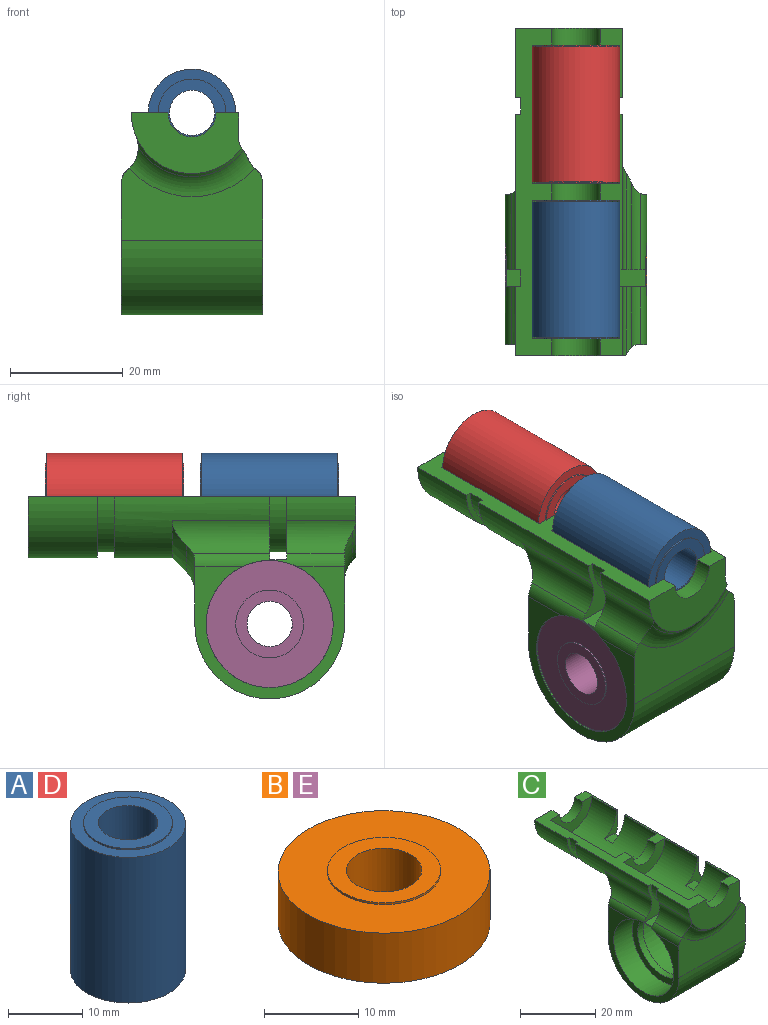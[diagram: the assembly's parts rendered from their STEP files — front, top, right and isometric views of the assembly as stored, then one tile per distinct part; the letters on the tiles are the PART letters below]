
ASSEMBLY  parts=5 mates=4
PART A: 8 faces, bbox 15.5x15.5x24.5 mm
  f0: cylinder r=6mm len=12mm, axis (0,0,-1), area 9.4mm2, adj f4,f7
  f1: cylinder r=4mm len=24.5mm, axis (0,0,-1), area 615.8mm2, adj f3,f4
  f2: cylinder r=6mm len=12mm, axis (0,0,-1), area 9.4mm2, adj f3,f6
  f3: plane 12x12mm, normal (0,0,1), area 62.8mm2, adj f1,f2
  f4: plane 12x12mm, normal (0,0,-1), area 62.8mm2, adj f0,f1
  f5: cylinder r=7.75mm len=24mm, axis (0,0,-1), area 1168.7mm2, adj f6,f7
  f6: plane 15.5x15.5mm, normal (0,0,1), area 75.6mm2, adj f2,f5
  f7: plane 15.5x15.5mm, normal (0,0,-1), area 75.6mm2, adj f0,f5
PART B: 8 faces, bbox 22.5x22.5x7 mm
  f0: cylinder r=6mm len=12mm, axis (0,0,-1), area 9.4mm2, adj f4,f7
  f1: cylinder r=4mm len=8mm, axis (0,0,-1), area 175.9mm2, adj f3,f4
  f2: cylinder r=6mm len=12mm, axis (0,0,-1), area 9.4mm2, adj f3,f6
  f3: plane 12x12mm, normal (0,0,1), area 62.8mm2, adj f1,f2
  f4: plane 12x12mm, normal (0,0,-1), area 62.8mm2, adj f0,f1
  f5: cylinder r=11.25mm len=22.5mm, axis (0,0,-1), area 459.5mm2, adj f6,f7
  f6: plane 22.5x22.5mm, normal (0,0,1), area 284.5mm2, adj f2,f5
  f7: plane 22.5x22.5mm, normal (0,0,-1), area 284.5mm2, adj f0,f5
PART C: 60 faces, bbox 32.8x58x35.8 mm
  f0: cylinder r=9.75mm len=16.54mm, axis (0,-1,0), area 68.5mm2, adj f5,f13,f28,f53
  f1: plane 19x10.75mm, normal (0,1,0), area 140.7mm2, adj f14,f15,f27,f28,f52,f57
  f2: plane 19.52x10.75mm, normal (0,-1,0), area 141.8mm2, adj f6,f23,f24,f28,f42,f49,f55
  f3: cylinder r=9.75mm len=16.54mm, axis (0,-1,0), area 68.5mm2, adj f4,f25,f28,f50
  f4: plane 24.45x11.15mm, normal (0,-1,0), area 84.8mm2, adj f3,f7,f9,f21,f26,f28,f31,f45
  f5: plane 19x10.75mm, normal (0,1,0), area 36mm2, adj f0,f7,f17,f26,f28,f51,f53,f54
  f6: plane 12.25x4mm, normal (0,0,1), area 16.6mm2, adj f2,f21,f22,f23,f25,f49
  f7: plane 27.5x4mm, normal (0,0,1), area 24.3mm2, adj f4,f5,f17,f18,f19,f20,f21,f51
  f8: torus R=14.82mm, axis (0,-1,0), area 90.2mm2, adj f10,f30,f42,f46,f59
  f9: cylinder r=5mm len=15.39mm, axis (0,-1,0), area 38.4mm2, adj f4,f43,f44,f47,f58
  f10: cylinder r=5mm len=10.77mm, axis (0,-1,0), area 27.9mm2, adj f8,f25,f30,f47,f59
  f11: cylinder r=9.25mm len=18.5mm, axis (-1,0,0), area 116.2mm2, adj f37,f39
  f12: cylinder r=11.25mm len=22.5mm, axis (-1,0,0), area 493.5mm2, adj f34,f37,f48
  f13: plane 19x10.75mm, normal (0,-1,0), area 36mm2, adj f0,f14,f17,f27,f28,f52,f53,f57
  f14: cylinder r=10.75mm len=16.83mm, axis (0,-1,0), area 286mm2, adj f1,f13,f28,f57
  f15: cylinder r=4.25mm len=8.5mm, axis (0,-1,0), area 40.1mm2, adj f1,f16,f27,f28
  f16: plane 15.5x7.75mm, normal (0,-1,0), area 66mm2, adj f15,f17,f27,f28
  f17: cylinder r=7.75mm len=24.5mm, axis (0,-1,0), area 570.3mm2, adj f5,f7,f13,f16,f18,f27,f28,f53
  f18: plane 15.5x7.75mm, normal (0,1,0), area 66mm2, adj f7,f17,f19,f28
  f19: cylinder r=4.25mm len=8.5mm, axis (0,-1,0), area 40.1mm2, adj f7,f18,f20,f28
  f20: plane 15.5x7.75mm, normal (0,-1,0), area 66mm2, adj f7,f19,f21,f28
  f21: cylinder r=7.75mm len=24.5mm, axis (0,-1,0), area 570.3mm2, adj f4,f6,f7,f20,f22,f25,f28,f50
  f22: plane 15.5x7.75mm, normal (0,1,0), area 66mm2, adj f6,f21,f23,f28
  f23: cylinder r=4.25mm len=8.5mm, axis (0,-1,0), area 40.1mm2, adj f2,f6,f22,f28
  f24: cylinder r=10.75mm len=12.25mm, axis (0,-1,0), area 52.9mm2, adj f2,f25,f28,f46
  f25: plane 24.45x11.15mm, normal (0,1,0), area 84.8mm2, adj f3,f6,f10,f21,f24,f28,f31,f46
  f26: cylinder r=10.75mm len=27.5mm, axis (0,-1,0), area 313.8mm2, adj f4,f5,f28,f43,f45,f56
  f27: plane 12.25x4mm, normal (0,0,1), area 16.6mm2, adj f1,f13,f15,f16,f17,f52
  f28: plane 58x6.5mm, normal (0,0,1), area 199.5mm2, adj f0,f1,f2,f3,f4,f5,f13,f14
  f29: plane 25x11.07mm, normal (0,1,0), area 184.6mm2, adj f33,f34,f41,f44,f47,f48
  f30: plane 25x12.68mm, normal (0,-1,0), area 237.8mm2, adj f8,f10,f33,f34,f41,f46,f47,f48
  f31: plane 24.45x3mm, normal (0,0,1), area 73.3mm2, adj f4,f25,f47,f48
  f32: cylinder r=11.25mm len=22.5mm, axis (-1,0,0), area 493.5mm2, adj f33,f36,f47
  f33: plane 26.5x23.34mm, normal (1,0,0), area 153.4mm2, adj f29,f30,f32,f41,f47
  f34: plane 26.5x23.34mm, normal (-1,0,0), area 153.4mm2, adj f12,f29,f30,f41,f48
  f35: cylinder r=9.25mm len=18.5mm, axis (-1,0,0), area 116.2mm2, adj f36,f40
  f36: plane 22.5x22.5mm, normal (1,0,0), area 128.8mm2, adj f32,f35
  f37: plane 22.5x22.5mm, normal (-1,0,0), area 128.8mm2, adj f11,f12
  f38: cylinder r=11.25mm len=22.5mm, axis (1,0,0), area 494.8mm2, adj f39,f40
  f39: plane 22.5x22.5mm, normal (1,0,0), area 128.8mm2, adj f11,f38
  f40: plane 22.5x22.5mm, normal (-1,0,0), area 128.8mm2, adj f35,f38
  f41: cylinder r=13.25mm len=26.5mm, axis (1,0,0), area 1040.7mm2, adj f29,f30,f33,f34
  f42: cone r=12.75mm half-angle=45deg, axis (0,1,0), area 16.7mm2, adj f2,f8,f46,f55,f59
  f43: cone r=10.75mm half-angle=45deg, axis (0,-1,0), area 81.5mm2, adj f9,f26,f44,f45,f54,f56,f58
  f44: torus R=16.82mm, axis (0,-1,0), area 99.4mm2, adj f9,f29,f43,f45,f47,f48
  f45: cylinder r=5mm len=17.25mm, axis (0,-1,0), area 101.6mm2, adj f4,f26,f43,f44,f48
  f46: cylinder r=5mm len=12.25mm, axis (0,-1,0), area 72.3mm2, adj f8,f24,f25,f30,f42,f48
  f47: cylinder r=3mm len=26.78mm, axis (0,-1,0), area 59.3mm2, adj f4,f9,f10,f25,f29,f30,f31,f32
  f48: cylinder r=3mm len=26.78mm, axis (0,-1,0), area 59.3mm2, adj f4,f12,f25,f29,f30,f31,f34,f44
  f49: plane 12.25x4.52mm, normal (1,0,0), area 55.3mm2, adj f2,f6,f25,f55
  f50: plane 3.46x3mm, normal (0,0,1), area 10.4mm2, adj f3,f4,f21,f25
  f51: plane 27.5x4.52mm, normal (1,0,0), area 124.2mm2, adj f4,f5,f7,f54
  f52: plane 12.25x4.74mm, normal (1,0,0), area 58.1mm2, adj f1,f13,f27,f57
  f53: plane 3.46x3mm, normal (0,0,1), area 10.4mm2, adj f0,f5,f13,f17
  f54: cylinder r=3mm len=27.5mm, axis (0,-1,0), area 38.3mm2, adj f4,f5,f43,f51,f56,f58
  f55: cylinder r=3mm len=12.25mm, axis (0,-1,0), area 25.7mm2, adj f2,f25,f42,f49,f59
  f56: cylinder r=5mm len=10.25mm, axis (0,-1,0), area 48.9mm2, adj f5,f26,f43,f54
  f57: cylinder r=5mm len=12.25mm, axis (0,-1,0), area 59.4mm2, adj f1,f13,f14,f52
  f58: cylinder r=5mm len=16.96mm, axis (0,-1,0), area 27.6mm2, adj f4,f9,f43,f54
  f59: cylinder r=5mm len=11.96mm, axis (0,-1,0), area 19.2mm2, adj f8,f10,f25,f42,f55
PART D: same geometry as A
PART E: same geometry as B
PLACE A rot(axis=(1,0,0),90deg) t=(4.9,-12.47,15.55)mm
PLACE B rot(axis=(0,1,0),90deg) t=(13.9,-12.47,-6.95)mm
PLACE C t=(4.9,-62.47,15.55)mm
PLACE D rot(axis=(1,0,0),90deg) t=(4.9,15.03,15.55)mm
PLACE E rot(axis=(0,-1,0),90deg) t=(-4.1,-12.47,-6.95)mm
MATE fastened D.f0 <-> C.f0  axis (0,1,0) through (4.9,2.78,15.55)mm
MATE fastened B.f0 <-> C.f11  axis (-1,0,0) through (10.4,-12.47,-6.95)mm
MATE fastened E.f0 <-> C.f11  axis (1,0,0) through (-0.6,-12.47,-6.95)mm
MATE fastened A.f0 <-> C.f0  axis (0,1,0) through (4.9,-0.22,15.55)mm
